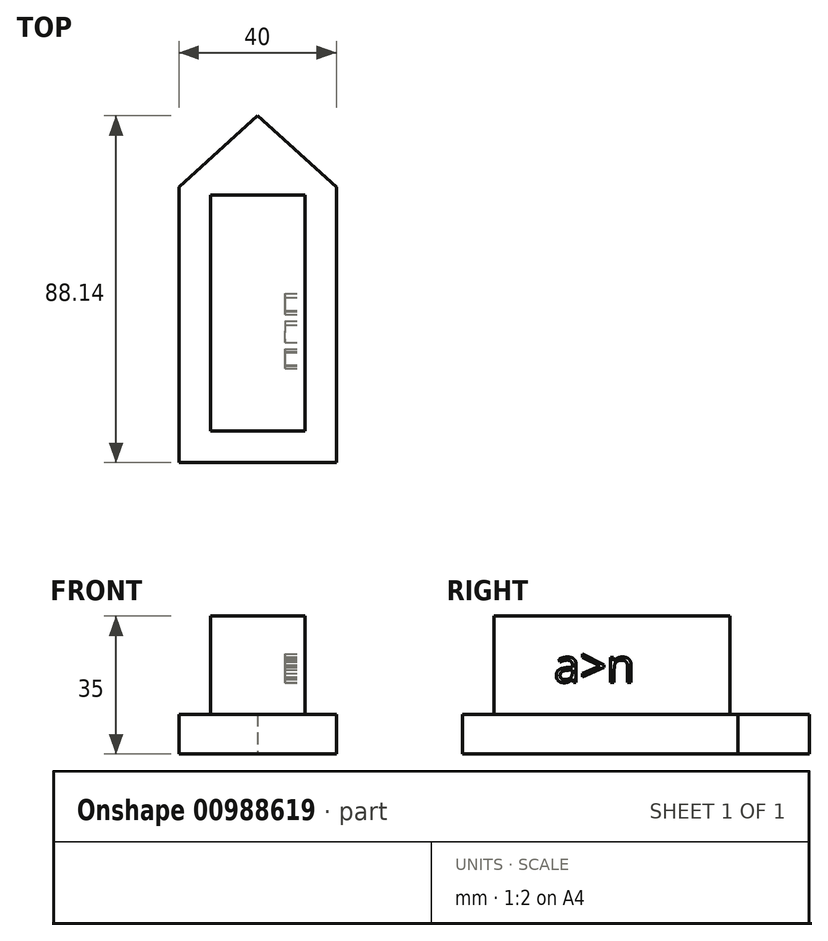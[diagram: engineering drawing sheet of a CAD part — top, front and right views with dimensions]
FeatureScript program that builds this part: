
annotation { "Feature Type Name" : "Feature", "Feature Type Description" : "" }
export const myFeature = defineFeature(function(context is Context, id is Id, definition is map)
    precondition{}
    {
        {
            var Q0;
            Q0=qCreatedBy(makeId("Top.planeOp"),FACE);
            var sketch = newSketch(context, id + "F0", { "sketchPlane" : qUnion([Q0])});
            skLineSegment(sketch, "E0", {"start": v(-9.97, 55.19) * mm, "end": v(-29.97, 37.05) * mm});
            skLineSegment(sketch, "E1", {"start": v(-29.97, 37.05) * mm, "end": v(-29.97, -32.95) * mm});
            skLineSegment(sketch, "E2", {"start": v(-29.97, -32.95) * mm, "end": v(10.03, -32.95) * mm});
            skLineSegment(sketch, "E3", {"start": v(10.03, -32.95) * mm, "end": v(10.03, 37.05) * mm});
            skLineSegment(sketch, "E4", {"start": v(10.03, 37.05) * mm, "end": v(-9.97, 55.19) * mm});
            skSolve(sketch);
        }
        {
            var Q0;
            Q0=makeQuery(id+"F0.imprint","IMPRINT",FACE,{"disambiguationData":[TD([[makeQuery(id+"F0.imprint","IMPRINT",EDGE,{"derivedFrom":sQuery(id+"F0.wireOp",EDGE,"E0")}),1.0]])]});
            extrude(context, id + "F1", {"entities" : qUnion([Q0]), "depth" : 10 * mm, "offsetDistance" : 25 * mm});
        }
        {
            var Q0;
            Q0=makeQuery(id+"F1.opExtrude","CAP_FACE",FACE,{"disambiguationData":[OSD([sQuery(id+"F0.wireOp",EDGE,"E0"),sQuery(id+"F0.wireOp",EDGE,"E1"),sQuery(id+"F0.wireOp",EDGE,"E2"),sQuery(id+"F0.wireOp",EDGE,"E3"),sQuery(id+"F0.wireOp",EDGE,"E4")])],"isStart":false});
            var sketch = newSketch(context, id + "F2", { "sketchPlane" : qUnion([Q0])});
            skLineSegment(sketch, "E5.bottom", {"start": v(-21.97, 35.05) * mm, "end": v(2.03, 35.05) * mm});
            skLineSegment(sketch, "E5.top", {"start": v(-21.97, -24.95) * mm, "end": v(2.03, -24.95) * mm});
            skLineSegment(sketch, "E5.left", {"start": v(-21.97, 35.05) * mm, "end": v(-21.97, -24.95) * mm});
            skLineSegment(sketch, "E5.right", {"start": v(2.03, 35.05) * mm, "end": v(2.03, -24.95) * mm});
            skSolve(sketch);
        }
        {
            var Q0;
            Q0 = qSketchRegion(id + "F2", true);
            extrude(context, id + "F3", {"entities" : qUnion([Q0]), "operationType" : NewBodyOperationType.ADD, "depth" : 25 * mm, "offsetDistance" : 25 * mm});
        }
        {
            var Q0;
            Q0=makeQuery(id+"F3.opExtrude","CAP_FACE",FACE,{"disambiguationData":[OSD([sQuery(id+"F2.wireOp",EDGE,"E5.bottom"),sQuery(id+"F2.wireOp",EDGE,"E5.top"),sQuery(id+"F2.wireOp",EDGE,"E5.left"),sQuery(id+"F2.wireOp",EDGE,"E5.right")])],"isStart":false});
            var sketch = newSketch(context, id + "F4", { "sketchPlane" : qUnion([Q0])});
            skCircle(sketch, "E6", {"center": v(-9.97, 27.05) * mm, "radius": 5.73 * mm});
            skCircle(sketch, "E7", {"center": v(-9.97, -16.95) * mm, "radius": 6.23 * mm});
            skCircle(sketch, "E8", {"center": v(-9.97, 5.05) * mm, "radius": 5.97 * mm});
            skPoint(sketch, "E8.centerSnap0", {"position": v(-21.97, 5.05) * mm});
            skSolve(sketch);
        }
        {
            var Q0;
            Q0 = qConstructionFilter(qBodyType(qCreatedBy(id + "F4" ,EDGE), BodyType.WIRE), ConstructionObject.NO);
            extrude(context, id + "F5", {"bodyType" : ToolBodyType.SURFACE, "surfaceEntities" : qUnion([Q0]), "depth" : 25 * mm, "offsetDistance" : 25 * mm});
        }
        {
            var Q0;
            Q0=makeQuery(id+"F3.opExtrude","SWEPT_FACE",FACE,{"disambiguationData":[OSD([sQuery(id+"F2.wireOp",EDGE,"E5.right")])]});
            var sketch = newSketch(context, id + "F6", { "sketchPlane" : qUnion([Q0])});
            skText(sketch, "E9", { "text": "a>n", "fontName": "OpenSans-Regular.ttf"});
            const initialGuessF6  = {"E9": [-0.00964, 0.01818, 1, 0, 0.00849]};
            skSetInitialGuess(sketch, initialGuessF6);
            skSolve(sketch);
        }
        {
            var Q0;
            Q0 = qSketchRegion(id + "F6", true);
            extrude(context, id + "F7", {"entities" : qUnion([Q0]), "operationType" : NewBodyOperationType.REMOVE, "oppositeDirection" : true, "depth" : 5 * mm, "offsetDistance" : 25 * mm});
        }
    });
